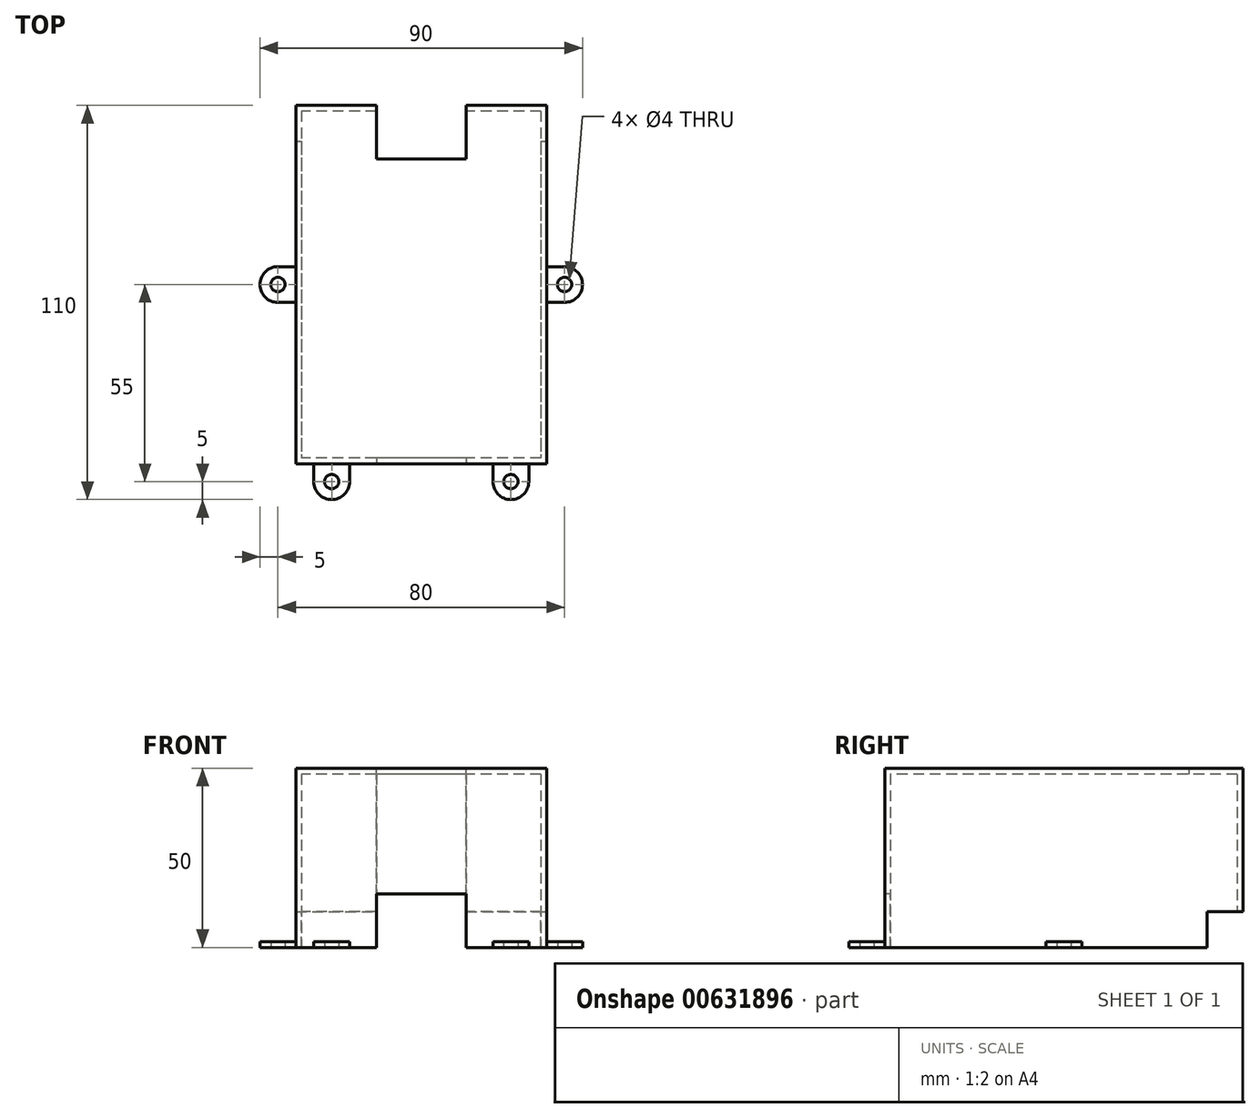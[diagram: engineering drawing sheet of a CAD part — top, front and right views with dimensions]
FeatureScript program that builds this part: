
annotation { "Feature Type Name" : "Feature", "Feature Type Description" : "" }
export const myFeature = defineFeature(function(context is Context, id is Id, definition is map)
    precondition{}
    {
        {
            var Q0;
            Q0=qCreatedBy(makeId("Top.planeOp"),FACE);
            var sketch = newSketch(context, id + "F0", { "sketchPlane" : qUnion([Q0])});
            skLineSegment(sketch, "E0.bottom", {"start": v(35, 50) * mm, "end": v(-35, 50) * mm});
            skLineSegment(sketch, "E0.top", {"start": v(35, -50) * mm, "end": v(-35, -50) * mm});
            skLineSegment(sketch, "E0.left", {"start": v(35, 50) * mm, "end": v(35, -50) * mm});
            skLineSegment(sketch, "E0.right", {"start": v(-35, 50) * mm, "end": v(-35, -50) * mm});
            skPoint(sketch, "E0.middle", {"position": v(0, 0) * mm});
            skSolve(sketch);
        }
        {
            var Q0;
            Q0 = qSketchRegion(id + "F0", true);
            extrude(context, id + "F1", {"entities" : qUnion([Q0]), "depth" : 50 * mm, "offsetDistance" : 25 * mm});
        }
        {
            var Q0;
            Q0=makeQuery(id+"F1.opExtrude","CAP_FACE",FACE,{"disambiguationData":[OSD([sQuery(id+"F0.wireOp",EDGE,"E0.bottom"),sQuery(id+"F0.wireOp",EDGE,"E0.top"),sQuery(id+"F0.wireOp",EDGE,"E0.left"),sQuery(id+"F0.wireOp",EDGE,"E0.right")])],"isStart":true});
            shell(context, id + "F2", {"entities" : qUnion([Q0]), "thickness" : 1.6 * mm});
        }
        {
            var Q0;
            Q0=makeQuery(id+"F1.opExtrude","SWEPT_FACE",FACE,{"disambiguationData":[OSD([sQuery(id+"F0.wireOp",EDGE,"E0.left")])]});
            var sketch = newSketch(context, id + "F3", { "sketchPlane" : qUnion([Q0])});
            skLineSegment(sketch, "E1.bottom", {"start": v(50, 0) * mm, "end": v(40, 0) * mm});
            skLineSegment(sketch, "E1.top", {"start": v(50, 10) * mm, "end": v(40, 10) * mm});
            skLineSegment(sketch, "E1.left", {"start": v(50, 0) * mm, "end": v(50, 10) * mm});
            skLineSegment(sketch, "E1.right", {"start": v(40, 0) * mm, "end": v(40, 10) * mm});
            skSolve(sketch);
        }
        {
            var Q0;
            Q0 = qSketchRegion(id + "F3", true);
            extrude(context, id + "F4", {"entities" : qUnion([Q0]), "operationType" : NewBodyOperationType.REMOVE, "endBound" : BoundingType.THROUGH_ALL, "oppositeDirection" : true, "depth" : 25 * mm, "offsetDistance" : 25 * mm});
        }
        {
            var Q0;
            Q0=qCreatedBy(makeId("Top.planeOp"),FACE);
            var sketch = newSketch(context, id + "F5", { "sketchPlane" : qUnion([Q0])});
            skLineSegment(sketch, "E2.bottom", {"start": v(35, -5) * mm, "end": v(45, -5) * mm});
            skLineSegment(sketch, "E2.top", {"start": v(35, 5) * mm, "end": v(45, 5) * mm});
            skLineSegment(sketch, "E2.left", {"start": v(35, -5) * mm, "end": v(35, 5) * mm});
            skLineSegment(sketch, "E2.right", {"start": v(45, -5) * mm, "end": v(45, 5) * mm});
            skPoint(sketch, "E2.middle", {"position": v(40, 0) * mm});
            skCircle(sketch, "E3", {"center": v(40, 0) * mm, "radius": 2 * mm});
            skLineSegment(sketch, "E4.MirrorCS", {"start": v(-35, -5) * mm, "end": v(-35, 5) * mm});
            skLineSegment(sketch, "E5.MirrorCS", {"start": v(-35, 5) * mm, "end": v(-45, 5) * mm});
            skLineSegment(sketch, "E6.MirrorCS", {"start": v(-45, -5) * mm, "end": v(-45, 5) * mm});
            skLineSegment(sketch, "E7.MirrorCS", {"start": v(-35, -5) * mm, "end": v(-45, -5) * mm});
            skCircle(sketch, "E8.MirrorC", {"center": v(-40, 0) * mm, "radius": 2 * mm});
            skLineSegment(sketch, "E9.bottom", {"start": v(-30, -50) * mm, "end": v(-20, -50) * mm});
            skLineSegment(sketch, "E9.top", {"start": v(-30, -60) * mm, "end": v(-20, -60) * mm});
            skLineSegment(sketch, "E9.left", {"start": v(-30, -50) * mm, "end": v(-30, -60) * mm});
            skLineSegment(sketch, "E9.right", {"start": v(-20, -50) * mm, "end": v(-20, -60) * mm});
            skPoint(sketch, "E9.middle", {"position": v(-25, -55) * mm});
            skCircle(sketch, "E10", {"center": v(-25, -55) * mm, "radius": 2 * mm});
            skLineSegment(sketch, "E11.MirrorCS", {"start": v(20, -50) * mm, "end": v(20, -60) * mm});
            skLineSegment(sketch, "E12.MirrorCS", {"start": v(30, -60) * mm, "end": v(20, -60) * mm});
            skLineSegment(sketch, "E13.MirrorCS", {"start": v(30, -50) * mm, "end": v(20, -50) * mm});
            skLineSegment(sketch, "E14.MirrorCS", {"start": v(30, -50) * mm, "end": v(30, -60) * mm});
            skPoint(sketch, "E15.MirrorP", {"position": v(25, -55) * mm});
            skCircle(sketch, "E16.MirrorC", {"center": v(25, -55) * mm, "radius": 2 * mm});
            skSolve(sketch);
        }
        {
            var Q0;
            Q0 = qSketchRegion(id + "F5", true);
            extrude(context, id + "F6", {"entities" : qUnion([Q0]), "operationType" : NewBodyOperationType.ADD, "depth" : 1.6 * mm, "offsetDistance" : 25 * mm});
        }
        {
            var Q0;
            Q0=makeQuery(id+"F6.opExtrude","SWEPT_EDGE",EDGE,{"disambiguationData":[OSD([sQuery(id+"F5.wireOp",EDGE,"E6.MirrorCS"),sQuery(id+"F5.wireOp",EDGE,"E7.MirrorCS")])]});
            var Q1;
            Q1=makeQuery(id+"F6.opExtrude","SWEPT_EDGE",EDGE,{"disambiguationData":[OSD([sQuery(id+"F5.wireOp",EDGE,"E5.MirrorCS"),sQuery(id+"F5.wireOp",EDGE,"E6.MirrorCS")])]});
            var Q2;
            Q2=makeQuery(id+"F6.opExtrude","SWEPT_EDGE",EDGE,{"disambiguationData":[OSD([sQuery(id+"F5.wireOp",EDGE,"E2.bottom"),sQuery(id+"F5.wireOp",EDGE,"E2.right")])]});
            var Q3;
            Q3=makeQuery(id+"F6.opExtrude","SWEPT_EDGE",EDGE,{"disambiguationData":[OSD([sQuery(id+"F5.wireOp",EDGE,"E2.top"),sQuery(id+"F5.wireOp",EDGE,"E2.right")])]});
            var Q4;
            Q4=makeQuery(id+"F6.opExtrude","SWEPT_EDGE",EDGE,{"disambiguationData":[OSD([sQuery(id+"F5.wireOp",EDGE,"E9.top"),sQuery(id+"F5.wireOp",EDGE,"E9.left")])]});
            var Q5;
            Q5=makeQuery(id+"F6.opExtrude","SWEPT_EDGE",EDGE,{"disambiguationData":[OSD([sQuery(id+"F5.wireOp",EDGE,"E9.top"),sQuery(id+"F5.wireOp",EDGE,"E9.right")])]});
            var Q6;
            Q6=makeQuery(id+"F6.opExtrude","SWEPT_EDGE",EDGE,{"disambiguationData":[OSD([sQuery(id+"F5.wireOp",EDGE,"E11.MirrorCS"),sQuery(id+"F5.wireOp",EDGE,"E12.MirrorCS")])]});
            var Q7;
            Q7=makeQuery(id+"F6.opExtrude","SWEPT_EDGE",EDGE,{"disambiguationData":[OSD([sQuery(id+"F5.wireOp",EDGE,"E12.MirrorCS"),sQuery(id+"F5.wireOp",EDGE,"E14.MirrorCS")])]});
            fillet(context, id + "F7", {"entities" : qUnion([Q0, Q1, Q2, Q3, Q4, Q5, Q6, Q7]), "radius" : 5 * mm, "tangentPropagation" : true, "allowEdgeOverflow" : false});
        }
        {
            var Q0;
            Q0=makeQuery(id+"F1.opExtrude","CAP_FACE",FACE,{"disambiguationData":[OSD([sQuery(id+"F0.wireOp",EDGE,"E0.bottom"),sQuery(id+"F0.wireOp",EDGE,"E0.top"),sQuery(id+"F0.wireOp",EDGE,"E0.left"),sQuery(id+"F0.wireOp",EDGE,"E0.right")])],"isStart":false});
            var sketch = newSketch(context, id + "F8", { "sketchPlane" : qUnion([Q0])});
            skLineSegment(sketch, "E17.bottom", {"start": v(12.5, 50) * mm, "end": v(-12.5, 50) * mm});
            skLineSegment(sketch, "E17.top", {"start": v(12.5, 35) * mm, "end": v(-12.5, 35) * mm});
            skLineSegment(sketch, "E17.left", {"start": v(12.5, 50) * mm, "end": v(12.5, 35) * mm});
            skLineSegment(sketch, "E17.right", {"start": v(-12.5, 50) * mm, "end": v(-12.5, 35) * mm});
            skPoint(sketch, "E17.middle", {"position": v(0, 42.5) * mm});
            skPoint(sketch, "E17.middle.positionSnap0", {"position": v(0, 50) * mm});
            skPoint(sketch, "E17.centerSnap0", {"position": v(0, 50) * mm});
            skSolve(sketch);
        }
        {
            var Q0;
            Q0 = qSketchRegion(id + "F8", true);
            extrude(context, id + "F9", {"entities" : qUnion([Q0]), "operationType" : NewBodyOperationType.REMOVE, "endBound" : BoundingType.THROUGH_ALL, "oppositeDirection" : true, "depth" : 25 * mm, "offsetDistance" : 25 * mm});
        }
        {
            var Q0;
            Q0=makeQuery(id+"F1.opExtrude","SWEPT_FACE",FACE,{"disambiguationData":[OSD([sQuery(id+"F0.wireOp",EDGE,"E0.top")])]});
            var sketch = newSketch(context, id + "F10", { "sketchPlane" : qUnion([Q0])});
            skLineSegment(sketch, "E18.bottom", {"start": v(12.5, 0) * mm, "end": v(-12.5, 0) * mm});
            skLineSegment(sketch, "E18.top", {"start": v(12.5, 15) * mm, "end": v(-12.5, 15) * mm});
            skLineSegment(sketch, "E18.left", {"start": v(12.5, 0) * mm, "end": v(12.5, 15) * mm});
            skLineSegment(sketch, "E18.right", {"start": v(-12.5, 0) * mm, "end": v(-12.5, 15) * mm});
            skPoint(sketch, "E18.middle", {"position": v(0, 7.5) * mm});
            skSolve(sketch);
        }
        {
            var Q0;
            Q0 = qSketchRegion(id + "F10", true);
            extrude(context, id + "F11", {"entities" : qUnion([Q0]), "operationType" : NewBodyOperationType.REMOVE, "endBound" : BoundingType.THROUGH_ALL, "oppositeDirection" : true, "depth" : 25 * mm, "offsetDistance" : 25 * mm});
        }
    });
